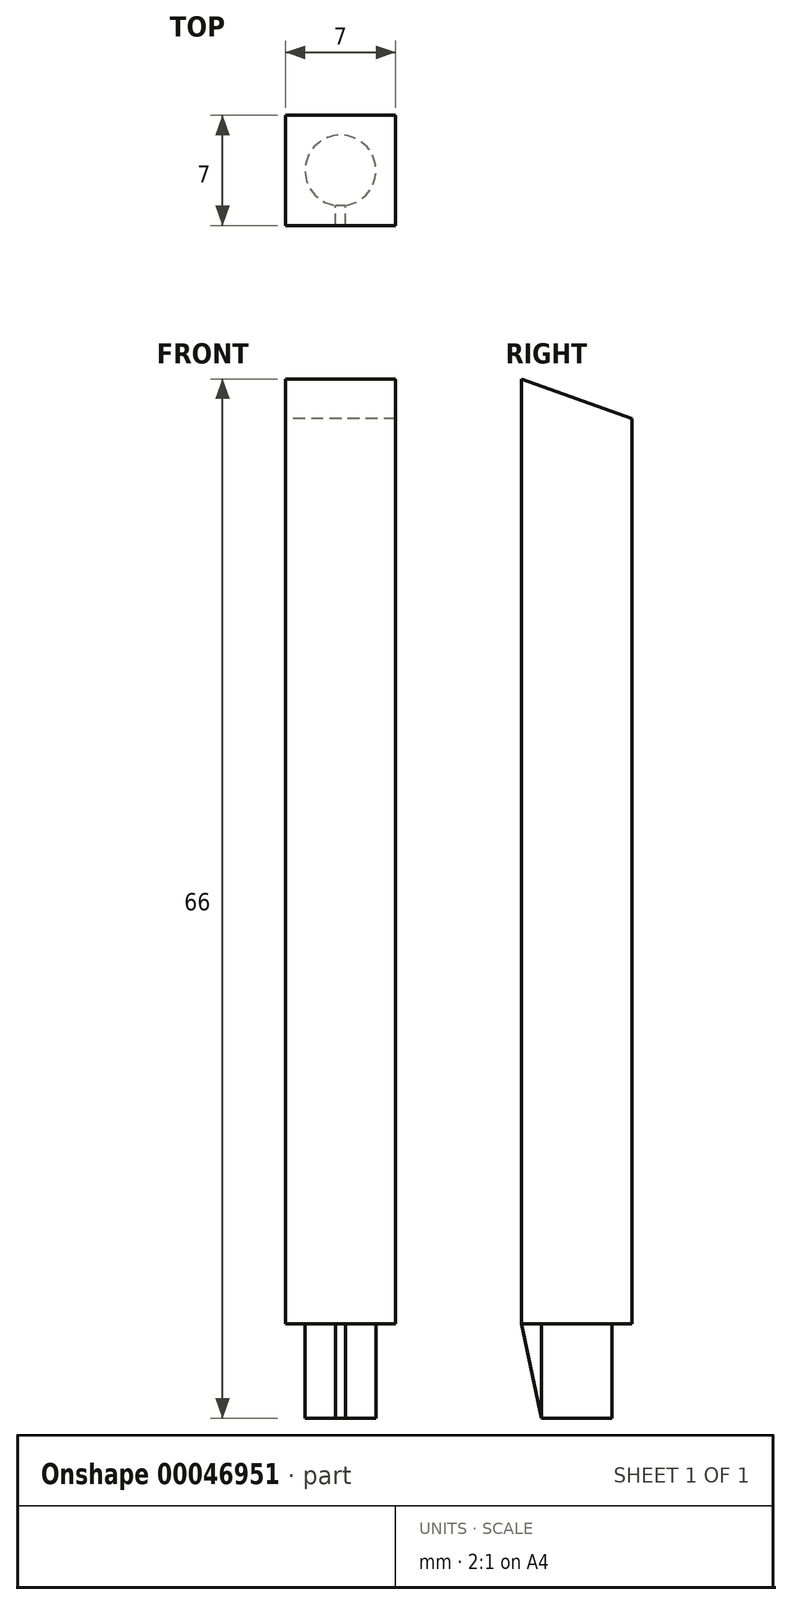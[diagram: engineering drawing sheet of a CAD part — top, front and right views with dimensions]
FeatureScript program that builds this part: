
annotation { "Feature Type Name" : "Feature", "Feature Type Description" : "" }
export const myFeature = defineFeature(function(context is Context, id is Id, definition is map)
    precondition{}
    {
        {
            var Q0;
            Q0=qCreatedBy(makeId("Top.planeOp"),FACE);
            var sketch = newSketch(context, id + "F0", { "sketchPlane" : qUnion([Q0])});
            skCircle(sketch, "E0", {"center": v(0, 0) * mm, "radius": 2.25 * mm});
            skLineSegment(sketch, "E1.bottom", {"start": v(-3.5, 3.5) * mm, "end": v(3.5, 3.5) * mm});
            skLineSegment(sketch, "E1.top", {"start": v(-3.5, -3.5) * mm, "end": v(3.5, -3.5) * mm});
            skLineSegment(sketch, "E1.left", {"start": v(-3.5, 3.5) * mm, "end": v(-3.5, -3.5) * mm});
            skLineSegment(sketch, "E1.right", {"start": v(3.5, 3.5) * mm, "end": v(3.5, -3.5) * mm});
            skLineSegment(sketch, "E2", {"start": v(-3.5, 3.5) * mm, "end": v(3.5, -3.5) * mm, "construction": true});
            skSolve(sketch);
        }
        {
            var Q0;
            Q0=makeQuery(id+"F0.imprint","IMPRINT",FACE,{"disambiguationData":[TD([[makeQuery(id+"F0.imprint","IMPRINT",EDGE,{"derivedFrom":sQuery(id+"F0.wireOp",EDGE,"E0")}),-1.0]])]});
            var Q1;
            Q1=makeQuery(id+"F0.imprint","IMPRINT",FACE,{"disambiguationData":[TD([[makeQuery(id+"F0.imprint","IMPRINT",EDGE,{"derivedFrom":sQuery(id+"F0.wireOp",EDGE,"E0")}),1.0]])]});
            extrude(context, id + "F1", {"entities" : qUnion([Q0, Q1]), "depth" : 60 * mm});
        }
        {
            var Q0;
            Q0=makeQuery(id+"F0.imprint","IMPRINT",FACE,{"disambiguationData":[TD([[makeQuery(id+"F0.imprint","IMPRINT",EDGE,{"derivedFrom":sQuery(id+"F0.wireOp",EDGE,"E0")}),1.0]])]});
            extrude(context, id + "F2", {"entities" : qUnion([Q0]), "operationType" : NewBodyOperationType.ADD, "oppositeDirection" : true, "depth" : 6 * mm});
        }
        {
            var Q0;
            Q0=makeQuery(id+"F1.opExtrude","SWEPT_FACE",FACE,{"disambiguationData":[OSD([sQuery(id+"F0.wireOp",EDGE,"E1.left")])]});
            var sketch = newSketch(context, id + "F3", { "sketchPlane" : qUnion([Q0])});
            skLineSegment(sketch, "E3", {"start": v(-3.5, 0) * mm, "end": v(-163.5, 0) * mm});
            skLineSegment(sketch, "E4", {"start": v(3.5, 60) * mm, "end": v(-163.5, 0) * mm});
            skSolve(sketch);
        }
        {
            var Q0;
            {var subQ1=sQuery(id+"F0.wireOp",EDGE,"E1.left");var subQ2=makeQuery(id+"F1.opExtrude","CAP_EDGE",EDGE,{"disambiguationData":[OSD([subQ1])],"isStart":false});Q0=makeQuery(id+"F3.imprint","IMPRINT",FACE,{"disambiguationData":[TD([[makeQuery(id+"F3.imprint","IMPRINT",EDGE,{"derivedFrom":subQ2}),-1.0]])]});}
            extrude(context, id + "F4", {"entities" : qUnion([Q0]), "operationType" : NewBodyOperationType.REMOVE, "oppositeDirection" : true, "depth" : 25 * mm});
        }
        {
            var Q0;
            Q0=makeQuery(id+"F2.opExtrude","CAP_FACE",FACE,{"disambiguationData":[OSD([sQuery(id+"F0.wireOp",EDGE,"E0")])],"isStart":false});
            var sketch = newSketch(context, id + "F5", { "sketchPlane" : qUnion([Q0])});
            skLineSegment(sketch, "E5.bottom", {"start": v(-0.32, 0) * mm, "end": v(0.32, 0) * mm});
            skLineSegment(sketch, "E5.top", {"start": v(-0.32, 3.5) * mm, "end": v(0.32, 3.5) * mm});
            skLineSegment(sketch, "E5.left", {"start": v(-0.32, 0) * mm, "end": v(-0.32, 3.5) * mm});
            skLineSegment(sketch, "E5.right", {"start": v(0.32, 0) * mm, "end": v(0.32, 3.5) * mm});
            skPoint(sketch, "E6", {"position": v(0, 0) * mm});
            skSolve(sketch);
        }
        {
            var Q0;
            Q0 = qSketchRegion(id + "F5", true);
            extrude(context, id + "F6", {"entities" : qUnion([Q0]), "operationType" : NewBodyOperationType.ADD, "endBound" : BoundingType.UP_TO_NEXT, "oppositeDirection" : true, "depth" : 25 * mm});
        }
        {
            var Q0;
            Q0=makeQuery(id+"F6.opExtrude","SWEPT_FACE",FACE,{"disambiguationData":[OSD([sQuery(id+"F5.wireOp",EDGE,"E5.left")])]});
            var sketch = newSketch(context, id + "F7", { "sketchPlane" : qUnion([Q0])});
            skLineSegment(sketch, "E7", {"start": v(2.23, -6) * mm, "end": v(3.5, 0) * mm});
            skSolve(sketch);
        }
        {
            var Q0;
            Q0=makeQuery(id+"F7.imprint","IMPRINT",FACE,{"disambiguationData":[TD([[makeQuery(id+"F7.imprint","IMPRINT",EDGE,{"derivedFrom":sQuery(id+"F7.wireOp",EDGE,"E7")}),-1.0]])]});
            extrude(context, id + "F8", {"entities" : qUnion([Q0]), "operationType" : NewBodyOperationType.REMOVE, "oppositeDirection" : true, "depth" : 25 * mm});
        }
    });
